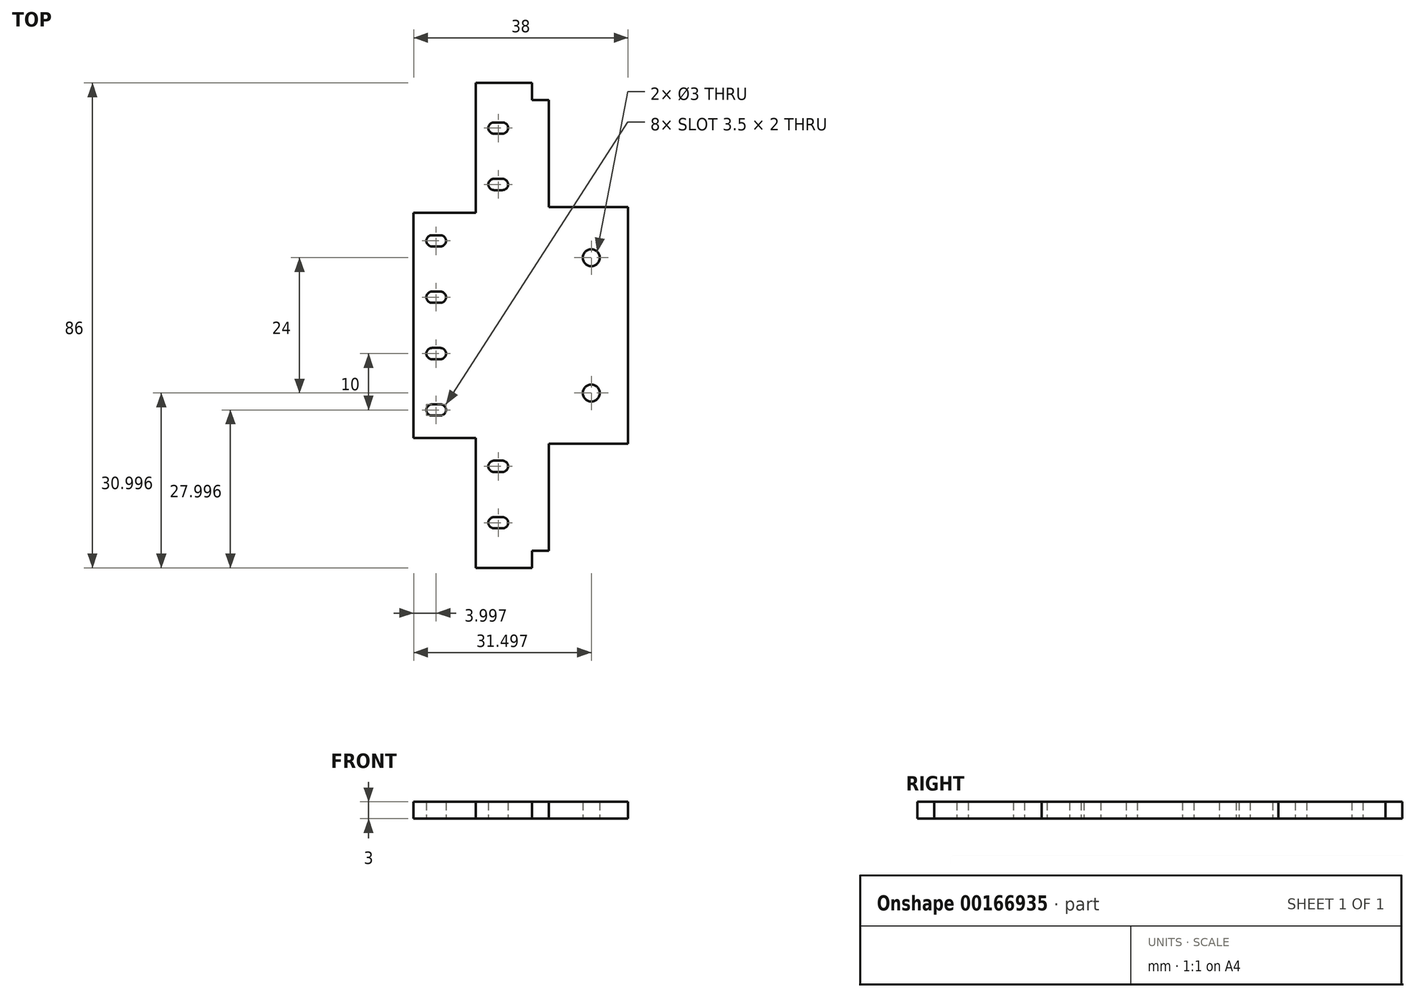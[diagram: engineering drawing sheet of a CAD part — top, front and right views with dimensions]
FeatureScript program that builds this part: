
annotation { "Feature Type Name" : "Feature", "Feature Type Description" : "" }
export const myFeature = defineFeature(function(context is Context, id is Id, definition is map)
    precondition{}
    {
        {
            var Q0;
            Q0=qCreatedBy(makeId("Top.planeOp"),FACE);
            var sketch = newSketch(context, id + "F0", { "sketchPlane" : qUnion([Q0])});
            skLineSegment(sketch, "E0", {"start": v(9.4, 3.28) * mm, "end": v(19.4, 3.28) * mm});
            skLineSegment(sketch, "E1", {"start": v(19.4, 3.28) * mm, "end": v(19.4, 6.28) * mm});
            skLineSegment(sketch, "E2", {"start": v(19.4, 6.28) * mm, "end": v(22.4, 6.28) * mm});
            skLineSegment(sketch, "E3", {"start": v(22.4, 6.28) * mm, "end": v(22.4, 25.28) * mm});
            skLineSegment(sketch, "E4", {"start": v(22.4, 25.28) * mm, "end": v(36.4, 25.28) * mm});
            skLineSegment(sketch, "E5", {"start": v(36.4, 25.28) * mm, "end": v(36.4, 67.28) * mm});
            skLineSegment(sketch, "E6", {"start": v(36.4, 67.28) * mm, "end": v(22.4, 67.28) * mm});
            skLineSegment(sketch, "E7", {"start": v(22.4, 67.28) * mm, "end": v(22.4, 86.28) * mm});
            skLineSegment(sketch, "E8", {"start": v(22.4, 86.28) * mm, "end": v(19.4, 86.28) * mm});
            skLineSegment(sketch, "E9", {"start": v(19.4, 86.28) * mm, "end": v(19.4, 89.28) * mm});
            skLineSegment(sketch, "E10", {"start": v(19.4, 89.28) * mm, "end": v(9.4, 89.28) * mm});
            skLineSegment(sketch, "E11", {"start": v(9.4, 89.28) * mm, "end": v(9.4, 66.28) * mm});
            skLineSegment(sketch, "E12", {"start": v(9.4, 66.28) * mm, "end": v(-1.6, 66.28) * mm});
            skLineSegment(sketch, "E13", {"start": v(-1.6, 66.28) * mm, "end": v(-1.6, 26.28) * mm});
            skLineSegment(sketch, "E14", {"start": v(-1.6, 26.28) * mm, "end": v(9.4, 26.28) * mm});
            skLineSegment(sketch, "E15", {"start": v(9.4, 26.28) * mm, "end": v(9.4, 3.28) * mm});
            skArc(sketch, "E16", {"start": v(0.65, 31.28) * mm, "mid": v(0.94, 30.57) * mm, "end": v(1.65, 30.28) * mm});
            skLineSegment(sketch, "E17", {"start": v(1.65, 30.28) * mm, "end": v(3.15, 30.28) * mm});
            skArc(sketch, "E18", {"start": v(3.15, 30.28) * mm, "mid": v(3.85, 30.57) * mm, "end": v(4.15, 31.28) * mm});
            skArc(sketch, "E19", {"start": v(4.15, 31.28) * mm, "mid": v(3.85, 31.98) * mm, "end": v(3.15, 32.28) * mm});
            skLineSegment(sketch, "E20", {"start": v(3.15, 32.28) * mm, "end": v(1.65, 32.28) * mm});
            skArc(sketch, "E21", {"start": v(1.65, 32.28) * mm, "mid": v(0.94, 31.98) * mm, "end": v(0.65, 31.28) * mm});
            skArc(sketch, "E22", {"start": v(0.65, 41.28) * mm, "mid": v(0.94, 40.57) * mm, "end": v(1.65, 40.28) * mm});
            skLineSegment(sketch, "E23", {"start": v(1.65, 40.28) * mm, "end": v(3.15, 40.28) * mm});
            skArc(sketch, "E24", {"start": v(3.15, 40.28) * mm, "mid": v(3.85, 40.57) * mm, "end": v(4.15, 41.28) * mm});
            skArc(sketch, "E25", {"start": v(4.15, 41.28) * mm, "mid": v(3.85, 41.98) * mm, "end": v(3.15, 42.28) * mm});
            skLineSegment(sketch, "E26", {"start": v(3.15, 42.28) * mm, "end": v(1.65, 42.28) * mm});
            skArc(sketch, "E27", {"start": v(1.65, 42.28) * mm, "mid": v(0.94, 41.98) * mm, "end": v(0.65, 41.28) * mm});
            skArc(sketch, "E28", {"start": v(0.65, 51.28) * mm, "mid": v(0.94, 50.57) * mm, "end": v(1.65, 50.28) * mm});
            skLineSegment(sketch, "E29", {"start": v(1.65, 50.28) * mm, "end": v(3.15, 50.28) * mm});
            skArc(sketch, "E30", {"start": v(3.15, 50.28) * mm, "mid": v(3.85, 50.57) * mm, "end": v(4.15, 51.28) * mm});
            skArc(sketch, "E31", {"start": v(4.15, 51.28) * mm, "mid": v(3.85, 51.98) * mm, "end": v(3.15, 52.28) * mm});
            skLineSegment(sketch, "E32", {"start": v(3.15, 52.28) * mm, "end": v(1.65, 52.28) * mm});
            skArc(sketch, "E33", {"start": v(1.65, 52.28) * mm, "mid": v(0.94, 51.98) * mm, "end": v(0.65, 51.28) * mm});
            skArc(sketch, "E34", {"start": v(0.65, 61.28) * mm, "mid": v(0.94, 60.57) * mm, "end": v(1.65, 60.28) * mm});
            skLineSegment(sketch, "E35", {"start": v(1.65, 60.28) * mm, "end": v(3.15, 60.28) * mm});
            skArc(sketch, "E36", {"start": v(3.15, 60.28) * mm, "mid": v(3.85, 60.57) * mm, "end": v(4.15, 61.28) * mm});
            skArc(sketch, "E37", {"start": v(4.15, 61.28) * mm, "mid": v(3.85, 61.98) * mm, "end": v(3.15, 62.28) * mm});
            skLineSegment(sketch, "E38", {"start": v(3.15, 62.28) * mm, "end": v(1.65, 62.28) * mm});
            skArc(sketch, "E39", {"start": v(1.65, 62.28) * mm, "mid": v(0.94, 61.98) * mm, "end": v(0.65, 61.28) * mm});
            skCircle(sketch, "E40", {"center": v(29.9, 58.28) * mm, "radius": 1.5 * mm});
            skCircle(sketch, "E41", {"center": v(29.9, 34.28) * mm, "radius": 1.5 * mm});
            skArc(sketch, "E42", {"start": v(11.65, 21.28) * mm, "mid": v(11.94, 20.57) * mm, "end": v(12.65, 20.28) * mm});
            skLineSegment(sketch, "E43", {"start": v(12.65, 20.28) * mm, "end": v(14.15, 20.28) * mm});
            skArc(sketch, "E44", {"start": v(14.15, 20.28) * mm, "mid": v(14.85, 20.57) * mm, "end": v(15.15, 21.28) * mm});
            skArc(sketch, "E45", {"start": v(15.15, 21.28) * mm, "mid": v(14.85, 21.98) * mm, "end": v(14.15, 22.28) * mm});
            skLineSegment(sketch, "E46", {"start": v(14.15, 22.28) * mm, "end": v(12.65, 22.28) * mm});
            skArc(sketch, "E47", {"start": v(12.65, 22.28) * mm, "mid": v(11.94, 21.98) * mm, "end": v(11.65, 21.28) * mm});
            skArc(sketch, "E48", {"start": v(11.65, 11.28) * mm, "mid": v(11.94, 10.57) * mm, "end": v(12.65, 10.28) * mm});
            skLineSegment(sketch, "E49", {"start": v(12.65, 10.28) * mm, "end": v(14.15, 10.28) * mm});
            skArc(sketch, "E50", {"start": v(14.15, 10.28) * mm, "mid": v(14.85, 10.57) * mm, "end": v(15.15, 11.28) * mm});
            skArc(sketch, "E51", {"start": v(15.15, 11.28) * mm, "mid": v(14.85, 11.98) * mm, "end": v(14.15, 12.28) * mm});
            skLineSegment(sketch, "E52", {"start": v(14.15, 12.28) * mm, "end": v(12.65, 12.28) * mm});
            skArc(sketch, "E53", {"start": v(12.65, 12.28) * mm, "mid": v(11.94, 11.98) * mm, "end": v(11.65, 11.28) * mm});
            skArc(sketch, "E54", {"start": v(11.65, 81.28) * mm, "mid": v(11.94, 80.57) * mm, "end": v(12.65, 80.28) * mm});
            skLineSegment(sketch, "E55", {"start": v(12.65, 80.28) * mm, "end": v(14.15, 80.28) * mm});
            skArc(sketch, "E56", {"start": v(14.15, 80.28) * mm, "mid": v(14.85, 80.57) * mm, "end": v(15.15, 81.28) * mm});
            skArc(sketch, "E57", {"start": v(15.15, 81.28) * mm, "mid": v(14.85, 81.98) * mm, "end": v(14.15, 82.28) * mm});
            skLineSegment(sketch, "E58", {"start": v(14.15, 82.28) * mm, "end": v(12.65, 82.28) * mm});
            skArc(sketch, "E59", {"start": v(12.65, 82.28) * mm, "mid": v(11.94, 81.98) * mm, "end": v(11.65, 81.28) * mm});
            skArc(sketch, "E60", {"start": v(11.65, 71.28) * mm, "mid": v(11.94, 70.57) * mm, "end": v(12.65, 70.28) * mm});
            skLineSegment(sketch, "E61", {"start": v(12.65, 70.28) * mm, "end": v(14.15, 70.28) * mm});
            skArc(sketch, "E62", {"start": v(14.15, 70.28) * mm, "mid": v(14.85, 70.57) * mm, "end": v(15.15, 71.28) * mm});
            skArc(sketch, "E63", {"start": v(15.15, 71.28) * mm, "mid": v(14.85, 71.98) * mm, "end": v(14.15, 72.28) * mm});
            skLineSegment(sketch, "E64", {"start": v(14.15, 72.28) * mm, "end": v(12.65, 72.28) * mm});
            skArc(sketch, "E65", {"start": v(12.65, 72.28) * mm, "mid": v(11.94, 71.98) * mm, "end": v(11.65, 71.28) * mm});
            skSolve(sketch);
        }
        {
            var Q0;
            Q0=makeQuery(id+"F0.imprint","IMPRINT",FACE,{"disambiguationData":[TD([[makeQuery(id+"F0.imprint","IMPRINT",EDGE,{"derivedFrom":sQuery(id+"F0.wireOp",EDGE,"E0")}),1.0]])]});
            extrude(context, id + "F1", {"entities" : qUnion([Q0]), "endBound" : BoundingType.SYMMETRIC, "depth" : 3 * mm});
        }
    });
